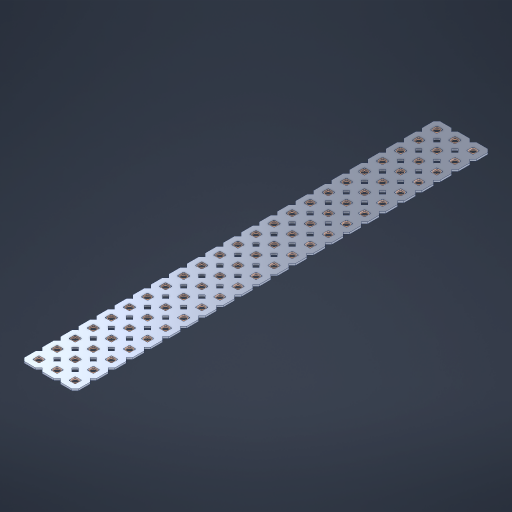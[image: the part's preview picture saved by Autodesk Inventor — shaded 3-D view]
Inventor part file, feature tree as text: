
AUTODESK INVENTOR PART (.ipt)
format: ipt  version: 2023 (Build 270158000, 158)  size: 1,055,744 bytes
history: native  units: in
note: dims shown in document units (in); Inventor stores cm internally (conversion verified against a paired STEP export)
features: other x70, extrude x68, sketch x2, pattern_linear x1
ambient origin geometry x8: Origin, YZ Plane, XZ Plane, XY Plane, X Axis, Y Axis, Z Axis, Center Point
bodies: Solid1 (feature_tree), Body (feature_tree)
feature tree (141):
  pattern_linear  "Rectangular Pattern1"  Spacing1=0.09in  [1 undecoded]
  sketch  "Sketch1"  dims[d1=0.5in]
  sketch  "Sketch2"  dims[d2=0.182in d3=0.09in d4=0.09in d5=0.09in d6=0.09in d7=0.09in d8=0.09in d9=0.09in d10=0.09in d11=0.02in d13=0.0in d14=0.172in d15=0.0625in d16=0.0in d19=0.5in d22=0.5in]
  other  "Srf1"
  other  "Srf126"
  other  "Srf127"
  other  "Srf128"
  other  "Srf129"
  other  "Srf130"
  other  "Srf131"
  other  "Srf250"
  other  "Srf251"
  other  "Srf252"
  other  "Srf253"
  other  "Srf254"
  other  "Srf255"
  other  "Srf256"
  other  "Srf257"
  other  "Srf258"
  other  "Srf259"
  other  "Srf260"
  other  "Srf261"
  other  "Srf262"
  other  "Srf263"
  other  "Srf264"
  other  "Srf265"
  other  "Srf268"
  other  "Srf269"
  other  "Srf270"
  other  "Srf271"
  other  "Srf272"
  other  "Srf273"
  other  "Srf274"
  other  "Srf275"
  other  "Srf276"
  other  "Srf277"
  other  "Srf278"
  other  "Srf279"
  other  "Srf280"
  other  "Srf281"
  other  "Srf282"
  other  "Srf283"
  other  "Srf284"
  other  "Srf285"
  other  "Srf286"
  other  "Srf287"
  other  "Srf288"
  other  "Srf289"
  other  "Srf290"
  other  "Srf293"
  other  "Srf294"
  other  "Srf295"
  other  "Srf296"
  other  "Srf297"
  other  "Srf298"
  other  "Srf299"
  other  "Srf300"
  other  "Srf301"
  other  "Srf302"
  other  "Srf303"
  other  "Srf304"
  other  "Srf305"
  other  "Srf306"
  other  "Srf307"
  other  "Srf308"
  other  "Srf309"
  other  "Srf310"
  other  "Srf311"
  other  "Srf312"
  other  "Srf313"
  other  "Srf314"
  other  "Srf315"
  other  "Circle"
  extrude  "ExtrusionSrf126"  Depth=0.09in
  extrude  "ExtrusionSrf127"  Depth=0.09in
  extrude  "ExtrusionSrf128"  Depth=0.09in
  extrude  "ExtrusionSrf129"  Depth=0.09in
  extrude  "ExtrusionSrf130"  Depth=0.09in
  extrude  "ExtrusionSrf131"  Depth=0.09in
  extrude  "ExtrusionSrf250"  Depth=0.09in
  extrude  "ExtrusionSrf251"  Depth=0.02in
  extrude  "ExtrusionSrf252"  TaperAngle=0.0deg  [1 undecoded]
  extrude  "ExtrusionSrf253"  Depth=0.5in
  extrude  "ExtrusionSrf254"  Depth=0.5in TaperAngle=0.0deg
  extrude  "ExtrusionSrf255"  Depth=0.5in
  extrude  "ExtrusionSrf256"  Depth=0.5in
  extrude  "ExtrusionSrf257"  [1 undecoded]
  extrude  "ExtrusionSrf258"  [1 undecoded]
  extrude  "ExtrusionSrf259"  [1 undecoded]
  extrude  "ExtrusionSrf260"  [1 undecoded]
  extrude  "ExtrusionSrf261"  [1 undecoded]
  extrude  "ExtrusionSrf262"  [1 undecoded]
  extrude  "ExtrusionSrf263"  [1 undecoded]
  extrude  "ExtrusionSrf264"  [1 undecoded]
  extrude  "ExtrusionSrf265"  [1 undecoded]
  extrude  "ExtrusionSrf268"  [1 undecoded]
  extrude  "ExtrusionSrf269"  [1 undecoded]
  extrude  "ExtrusionSrf270"  [1 undecoded]
  extrude  "ExtrusionSrf271"  [1 undecoded]
  extrude  "ExtrusionSrf272"  [1 undecoded]
  extrude  "ExtrusionSrf273"  [1 undecoded]
  extrude  "ExtrusionSrf274"  [1 undecoded]
  extrude  "ExtrusionSrf275"  [1 undecoded]
  extrude  "ExtrusionSrf276"  [1 undecoded]
  extrude  "ExtrusionSrf277"  [1 undecoded]
  extrude  "ExtrusionSrf278"  [1 undecoded]
  extrude  "ExtrusionSrf279"  [1 undecoded]
  extrude  "ExtrusionSrf280"  [1 undecoded]
  extrude  "ExtrusionSrf281"  [1 undecoded]
  extrude  "ExtrusionSrf282"  [1 undecoded]
  extrude  "ExtrusionSrf283"  [1 undecoded]
  extrude  "ExtrusionSrf284"  [1 undecoded]
  extrude  "ExtrusionSrf285"  [1 undecoded]
  extrude  "ExtrusionSrf286"  [1 undecoded]
  extrude  "ExtrusionSrf287"  [1 undecoded]
  extrude  "ExtrusionSrf288"  [1 undecoded]
  extrude  "ExtrusionSrf289"  [1 undecoded]
  extrude  "ExtrusionSrf290"  [1 undecoded]
  extrude  "ExtrusionSrf293"  [1 undecoded]
  extrude  "ExtrusionSrf294"  [1 undecoded]
  extrude  "ExtrusionSrf295"  [1 undecoded]
  extrude  "ExtrusionSrf296"  [1 undecoded]
  extrude  "ExtrusionSrf297"  [1 undecoded]
  extrude  "ExtrusionSrf298"  [1 undecoded]
  extrude  "ExtrusionSrf299"  [1 undecoded]
  extrude  "ExtrusionSrf300"  [1 undecoded]
  extrude  "ExtrusionSrf301"  [1 undecoded]
  extrude  "ExtrusionSrf302"  [1 undecoded]
  extrude  "ExtrusionSrf303"  [1 undecoded]
  extrude  "ExtrusionSrf304"  [1 undecoded]
  extrude  "ExtrusionSrf305"  [1 undecoded]
  extrude  "ExtrusionSrf306"  [1 undecoded]
  extrude  "ExtrusionSrf307"  [1 undecoded]
  extrude  "ExtrusionSrf308"  [1 undecoded]
  extrude  "ExtrusionSrf309"  [1 undecoded]
  extrude  "ExtrusionSrf310"  [1 undecoded]
  extrude  "ExtrusionSrf311"  [1 undecoded]
  extrude  "ExtrusionSrf312"  [1 undecoded]
  extrude  "ExtrusionSrf313"  [1 undecoded]
  extrude  "ExtrusionSrf314"  [1 undecoded]
  extrude  "ExtrusionSrf315"  [1 undecoded]
note: 57 required parameter values undecoded (feature->parameter linkage not recoverable at this tier; creation-order binding heuristic only, values carry confidence <= 0.55)
